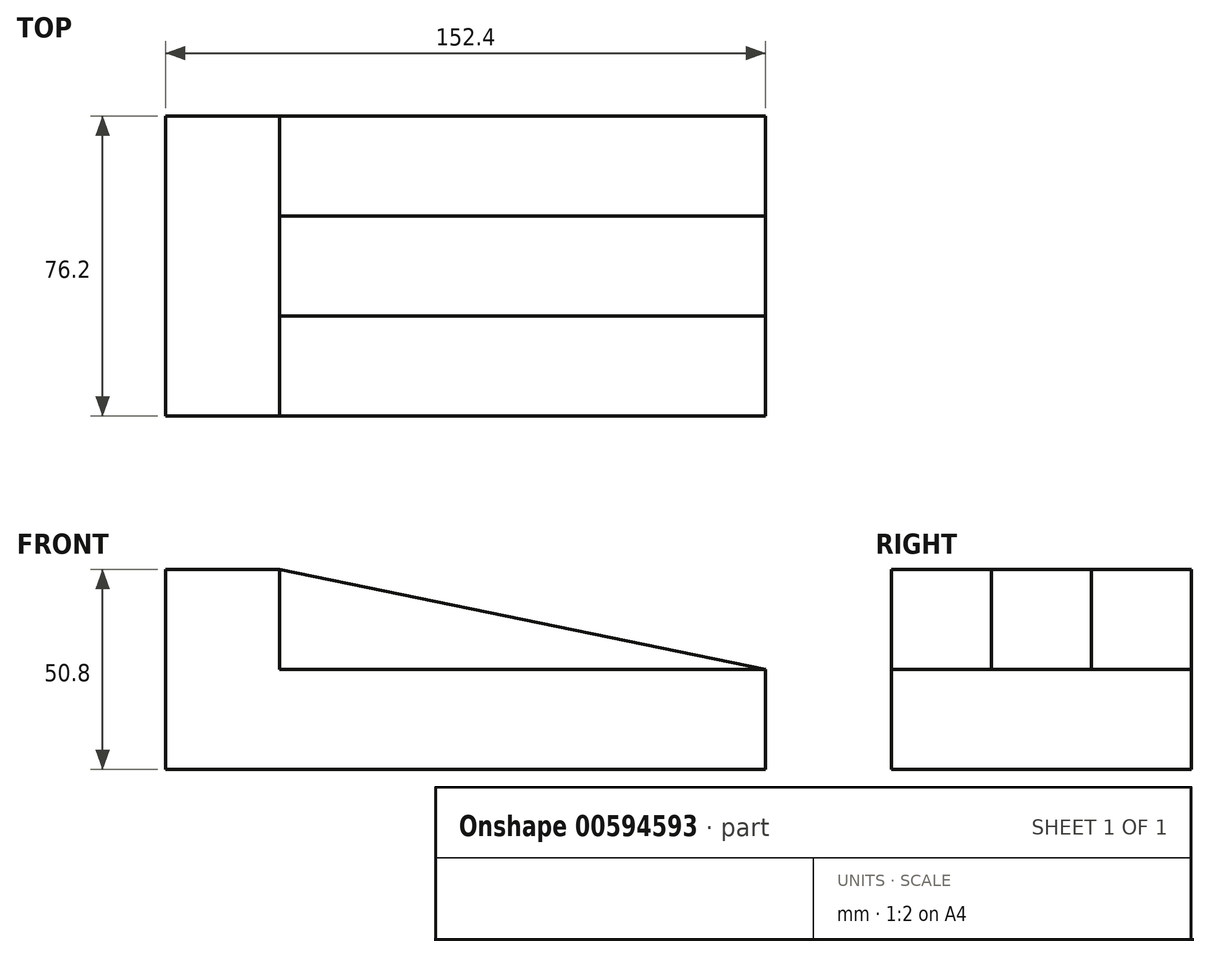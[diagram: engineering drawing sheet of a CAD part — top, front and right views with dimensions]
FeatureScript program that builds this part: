
annotation { "Feature Type Name" : "Feature", "Feature Type Description" : "" }
export const myFeature = defineFeature(function(context is Context, id is Id, definition is map)
    precondition{}
    {
        {
            var Q0;
            Q0=qCreatedBy(makeId("Front.planeOp"),FACE);
            var sketch = newSketch(context, id + "F0", { "sketchPlane" : qUnion([Q0])});
            skLineSegment(sketch, "E0.bottom", {"start": v(0, 0) * mm, "end": v(152.4, 0) * mm});
            skLineSegment(sketch, "E0.left", {"start": v(0, 0) * mm, "end": v(0, 50.8) * mm});
            skLineSegment(sketch, "E1", {"start": v(0, 50.8) * mm, "end": v(28.9, 50.8) * mm});
            skLineSegment(sketch, "E2", {"start": v(28.9, 50.8) * mm, "end": v(28.9, 25.4) * mm});
            skLineSegment(sketch, "E3", {"start": v(28.9, 25.4) * mm, "end": v(152.4, 25.4) * mm});
            skLineSegment(sketch, "E4", {"start": v(152.4, 0) * mm, "end": v(152.4, 25.4) * mm});
            skSolve(sketch);
        }
        {
            var Q0;
            Q0 = qSketchRegion(id + "F0", true);
            extrude(context, id + "F1", {"entities" : qUnion([Q0]), "oppositeDirection" : true, "depth" : 76.2 * mm, "offsetDistance" : 25.4 * mm});
        }
        {
            var Q0;
            Q0=makeQuery(id+"F1.opExtrude","CAP_FACE",FACE,{"disambiguationData":[OSD([sQuery(id+"F0.wireOp",EDGE,"E0.bottom"),sQuery(id+"F0.wireOp",EDGE,"E0.left"),sQuery(id+"F0.wireOp",EDGE,"E1"),sQuery(id+"F0.wireOp",EDGE,"E2"),sQuery(id+"F0.wireOp",EDGE,"E3"),sQuery(id+"F0.wireOp",EDGE,"E4")])],"isStart":true});
            var sketch = newSketch(context, id + "F2", { "sketchPlane" : qUnion([Q0])});
            skLineSegment(sketch, "E5", {"start": v(28.9, 50.8) * mm, "end": v(152.4, 25.4) * mm});
            skSolve(sketch);
        }
        {
            var Q0;
            Q0=makeQuery(id+"F2.imprint","IMPRINT",FACE,{"disambiguationData":[TD([[makeQuery(id+"F2.imprint","IMPRINT",EDGE,{"derivedFrom":sQuery(id+"F2.wireOp",EDGE,"E5")}),-1.0]])]});
            extrude(context, id + "F3", {"entities" : qUnion([Q0]), "operationType" : NewBodyOperationType.ADD, "oppositeDirection" : true, "depth" : 76.2 * mm, "offsetDistance" : 25.4 * mm});
        }
        {
            var Q0;
            {var subQ0=sQuery(id+"F0.wireOp",EDGE,"E3");var subQ1=sQuery(id+"F0.wireOp",EDGE,"E2");Q0=makeQuery(id+"F3.boolean.opBoolean","MERGE",FACE,{"derivedFrom":[makeQuery(id+"F1.opExtrude","CAP_FACE",FACE,{"disambiguationData":[OSD([sQuery(id+"F0.wireOp",EDGE,"E0.bottom"),sQuery(id+"F0.wireOp",EDGE,"E0.left"),sQuery(id+"F0.wireOp",EDGE,"E1"),subQ1,subQ0,sQuery(id+"F0.wireOp",EDGE,"E4")])],"isStart":true}),makeQuery(id+"F3.opExtrude","CAP_FACE",FACE,{"disambiguationData":[OSD([subQ1,subQ0,sQuery(id+"F2.wireOp",EDGE,"E5")])],"isStart":true})]});}
            var sketch = newSketch(context, id + "F4", { "sketchPlane" : qUnion([Q0])});
            skLineSegment(sketch, "E6", {"start": v(28.9, 50.8) * mm, "end": v(28.9, 25.4) * mm});
            skLineSegment(sketch, "E7", {"start": v(28.9, 25.4) * mm, "end": v(152.4, 25.4) * mm});
            skLineSegment(sketch, "E8", {"start": v(152.4, 25.4) * mm, "end": v(28.9, 50.8) * mm});
            skSolve(sketch);
        }
        {
            var Q0;
            Q0=makeQuery(id+"F4.imprint","IMPRINT",FACE,{"disambiguationData":[TD([[makeQuery(id+"F4.imprint","IMPRINT",EDGE,{"derivedFrom":sQuery(id+"F4.wireOp",EDGE,"E6")}),1.0]])]});
            extrude(context, id + "F5", {"entities" : qUnion([Q0]), "operationType" : NewBodyOperationType.REMOVE, "oppositeDirection" : true, "depth" : 25.4 * mm, "offsetDistance" : 25.4 * mm});
        }
        {
            var Q0;
            {var subQ0=sQuery(id+"F0.wireOp",EDGE,"E3");var subQ1=sQuery(id+"F0.wireOp",EDGE,"E2");Q0=makeQuery(id+"F3.boolean.opBoolean","MERGE",FACE,{"derivedFrom":[makeQuery(id+"F1.opExtrude","CAP_FACE",FACE,{"disambiguationData":[OSD([sQuery(id+"F0.wireOp",EDGE,"E0.bottom"),sQuery(id+"F0.wireOp",EDGE,"E0.left"),sQuery(id+"F0.wireOp",EDGE,"E1"),subQ1,subQ0,sQuery(id+"F0.wireOp",EDGE,"E4")])],"isStart":false}),makeQuery(id+"F3.opExtrude","CAP_FACE",FACE,{"disambiguationData":[OSD([subQ1,subQ0,sQuery(id+"F2.wireOp",EDGE,"E5")])],"isStart":false})]});}
            var sketch = newSketch(context, id + "F6", { "sketchPlane" : qUnion([Q0])});
            skLineSegment(sketch, "E9", {"start": v(-152.4, 25.4) * mm, "end": v(-28.9, 50.8) * mm});
            skLineSegment(sketch, "E10", {"start": v(-28.9, 50.8) * mm, "end": v(-28.9, 25.4) * mm});
            skLineSegment(sketch, "E11", {"start": v(-28.9, 25.4) * mm, "end": v(-152.4, 25.4) * mm});
            skSolve(sketch);
        }
        {
            var Q0;
            Q0 = qSketchRegion(id + "F6", true);
            extrude(context, id + "F7", {"entities" : qUnion([Q0]), "operationType" : NewBodyOperationType.REMOVE, "oppositeDirection" : true, "depth" : 25.4 * mm, "offsetDistance" : 25.4 * mm});
        }
    });
